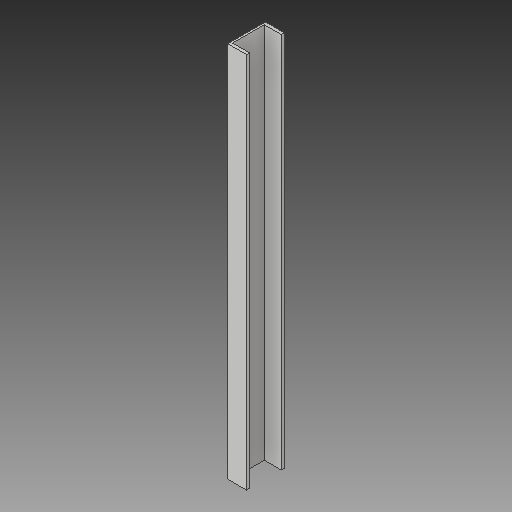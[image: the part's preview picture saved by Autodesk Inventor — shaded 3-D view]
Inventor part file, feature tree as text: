
AUTODESK INVENTOR PART (.ipt)
format: ipt  version: 2019 (Build 230136000, 136)  size: 89,600 bytes
history: native  units: in
note: dims shown in document units (in); Inventor stores cm internally (conversion verified against a paired STEP export)
features: other x3, sketch x1
ambient origin geometry x8: Origin, YZ Plane, XZ Plane, XY Plane, X Axis, Y Axis, Z Axis, Center Point
bodies: Solid1 (feature_tree)
feature tree (4):
  other  "Channel1.ipt"
  other  "Solid1::Channel1.ipt"
  other  "TaggingFeature1"
  sketch  "Sketch1"  dims[d0=0.3937in]
